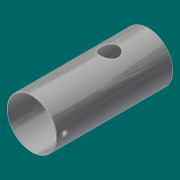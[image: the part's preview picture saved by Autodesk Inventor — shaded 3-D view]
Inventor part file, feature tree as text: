
AUTODESK INVENTOR PART (.ipt)
format: ipt  version: 2017.3 (Build 213257000, 257)  size: 299,520 bytes
history: native  units: in
note: dims shown in document units (in); Inventor stores cm internally (conversion verified against a paired STEP export)
features: extrude x7, split x5, other x5, sketch x4, plane x3, hole x3, pattern_circular x2, chamfer x2
ambient origin geometry x8: Origin, YZ Plane, XZ Plane, XY Plane, X Axis, Y Axis, Z Axis, Center Point
bodies: Solid1 (feature_tree)
feature tree (31):
  extrude  "Extrusion1"  Depth=35.25in
  plane  "Work Plane1"
  plane  "Work Plane2"
  sketch  "Sketch4"  dims[d2=84.6784in d3=0.0in d14=9.2291in]
  extrude  "Extrusion3"  Depth=84.6784in
  hole  "Hole1"  [1 undecoded]
  pattern_circular  "Circular Pattern1"  [2 undecoded]
  split  "Split1"
  split  "Split2"
  split  "Split3"
  split  "Split4"
  chamfer  "Chamfer1"  Distance=81.5359in
  hole  "Hole2"  [1 undecoded]
  pattern_circular  "Circular Pattern2"  [2 undecoded]
  plane  "Work Plane3"
  sketch  "Sketch6"  dims[d17=14.0in d18=46.9291in d19=81.5359in d20=0.0in d21=1.0in d22=0.0in d23=1.0in d24=0.0in d25=3.6875in d26=0.75in d27=0.375in d28=0.25in d29=0.5635in d30=1.0in d31=0.8108in d32=0.7874in d33=360.0deg d35=0.3125in d36=0.125in d37=0.2577in d38=5.9375in d39=0.688in d40=0.534in d41=0.0246in d42=0.688in d43=0.375in d44=0.25in d45=0.5635in d46=0.891in d47=0.8108in d48=1.1811in d49=135.0deg d51=4.125in d52=5.9063in d53=2.5625in d54=0.534in d55=0.375in d56=0.25in d57=0.5635in d58=0.891in d59=0.8108in d60=1.0in d61=0.0in d62=0.3125in d63=0.125in d64=0.2577in]
  hole  "Hole3"  [1 undecoded]
  split  "Split5"
  chamfer  "Chamfer2"  Distance=0.3125in
  sketch  "Sketch1"  dims[d0=36.0in d1=35.25in]
  other  "Srf1"
  other  "Srf2"
  other  "Srf3"
  other  "Srf4"
  sketch  "Sketch5"  dims[d15=5.25in d16=13.0in]
  other  "Srf5"
  extrude  "ExtrusionSrf1"  Depth=0.125in
  extrude  "ExtrusionSrf2"  Depth=5.9375in
  extrude  "ExtrusionSrf5"  Depth=1.1811in TaperAngle=135.0deg
  extrude  "ExtrusionSrf3"  Depth=4.125in
  extrude  "ExtrusionSrf4"  Depth=5.9063in
note: 7 required parameter values undecoded (feature->parameter linkage not recoverable at this tier; creation-order binding heuristic only, values carry confidence <= 0.55)
